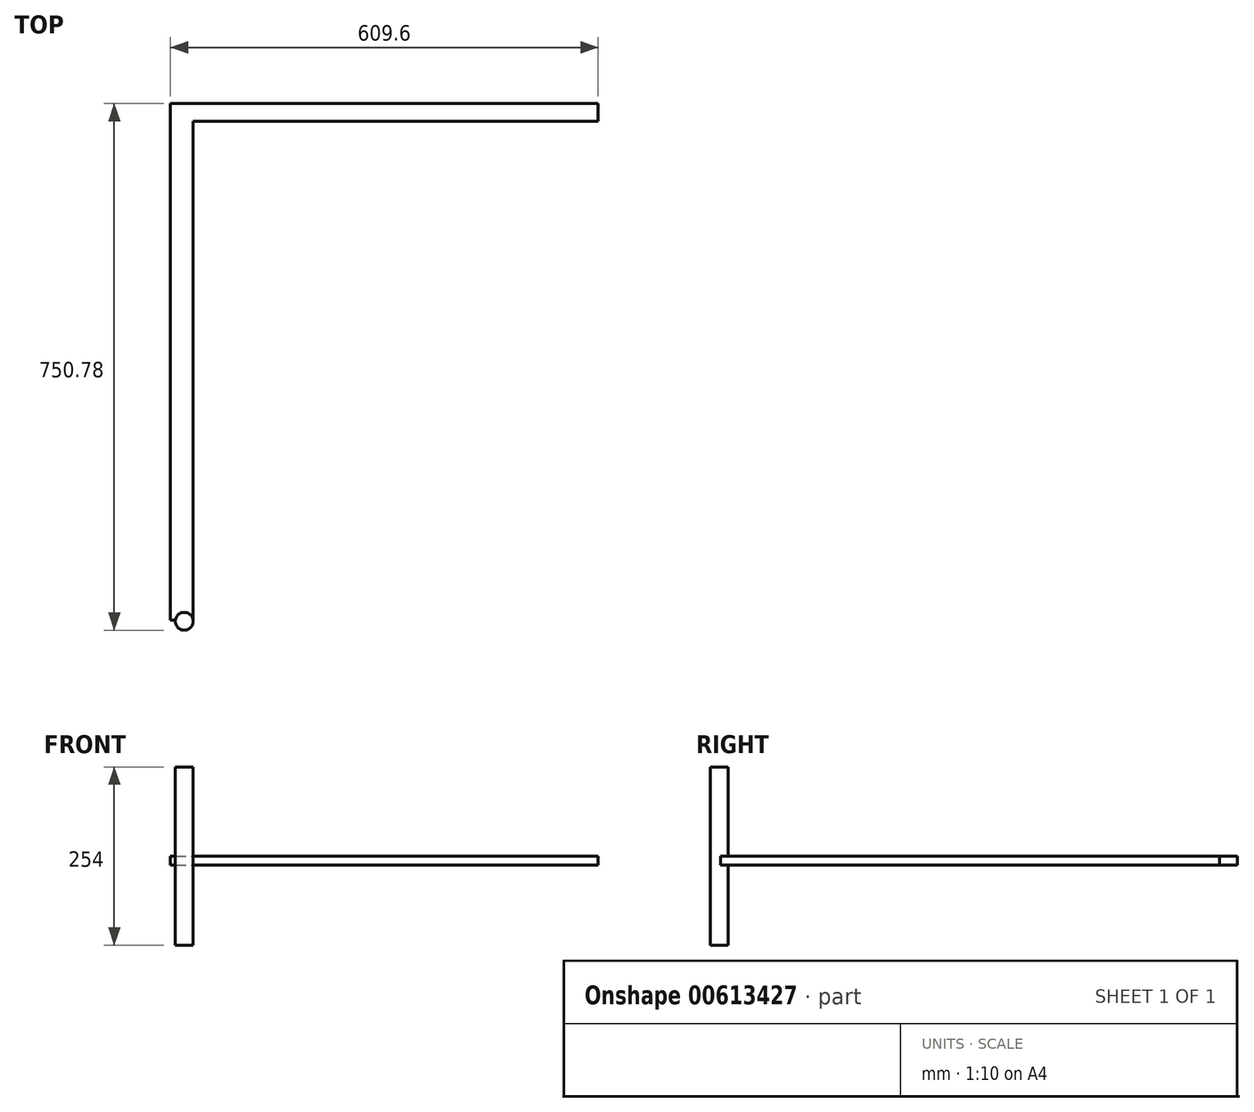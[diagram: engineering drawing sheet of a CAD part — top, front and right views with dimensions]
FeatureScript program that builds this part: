
annotation { "Feature Type Name" : "Feature", "Feature Type Description" : "" }
export const myFeature = defineFeature(function(context is Context, id is Id, definition is map)
    precondition{}
    {
        {
            var Q0;
            Q0=qCreatedBy(makeId("Top.planeOp"),FACE);
            var sketch = newSketch(context, id + "F0", { "sketchPlane" : qUnion([Q0])});
            skCircle(sketch, "E0", {"center": v(-12.7, 44.46) * mm, "radius": 12.7 * mm});
            skSolve(sketch);
        }
        {
            var Q0;
            Q0 = qSketchRegion(id + "F0", true);
            extrude(context, id + "F1", {"entities" : qUnion([Q0]), "oppositeDirection" : true, "depth" : 254 * mm, "offsetDistance" : 25.4 * mm});
        }
        {
            var Q0;
            Q0=qCreatedBy(makeId("Right.planeOp"),FACE);
            var sketch = newSketch(context, id + "F2", { "sketchPlane" : qUnion([Q0])});
            skLineSegment(sketch, "E1.bottom", {"start": v(45.94, -127.3) * mm, "end": v(757.14, -127.3) * mm});
            skLineSegment(sketch, "E1.top", {"start": v(45.94, -140) * mm, "end": v(757.14, -140) * mm});
            skLineSegment(sketch, "E1.left", {"start": v(45.94, -127.3) * mm, "end": v(45.94, -140) * mm});
            skLineSegment(sketch, "E1.right", {"start": v(757.14, -127.3) * mm, "end": v(757.14, -140) * mm});
            skSolve(sketch);
        }
        {
            var Q0;
            Q0=makeQuery(id+"F2.imprint","IMPRINT",FACE,{"disambiguationData":[TD([[makeQuery(id+"F2.imprint","IMPRINT",EDGE,{"derivedFrom":sQuery(id+"F2.wireOp",EDGE,"E1.bottom")}),-1.0]])]});
            extrude(context, id + "F3", {"entities" : qUnion([Q0]), "operationType" : NewBodyOperationType.ADD, "oppositeDirection" : true, "depth" : 32.26 * mm, "offsetDistance" : 25.4 * mm});
        }
        {
            var Q0;
            Q0=makeQuery(id+"F3.opExtrude","SWEPT_FACE",FACE,{"disambiguationData":[OSD([sQuery(id+"F2.wireOp",EDGE,"E1.right")])]});
            var sketch = newSketch(context, id + "F4", { "sketchPlane" : qUnion([Q0])});
            skLineSegment(sketch, "E2.bottom", {"start": v(32.26, -127.3) * mm, "end": v(-577.34, -127.3) * mm});
            skLineSegment(sketch, "E2.top", {"start": v(32.26, -140) * mm, "end": v(-577.34, -140) * mm});
            skLineSegment(sketch, "E2.left", {"start": v(32.26, -127.3) * mm, "end": v(32.26, -140) * mm});
            skLineSegment(sketch, "E2.right", {"start": v(-577.34, -127.3) * mm, "end": v(-577.34, -140) * mm});
            skSolve(sketch);
        }
        {
            var Q0;
            Q0 = qSketchRegion(id + "F4", true);
            extrude(context, id + "F5", {"entities" : qUnion([Q0]), "operationType" : NewBodyOperationType.ADD, "depth" : 25.4 * mm, "offsetDistance" : 25.4 * mm});
        }
    });
